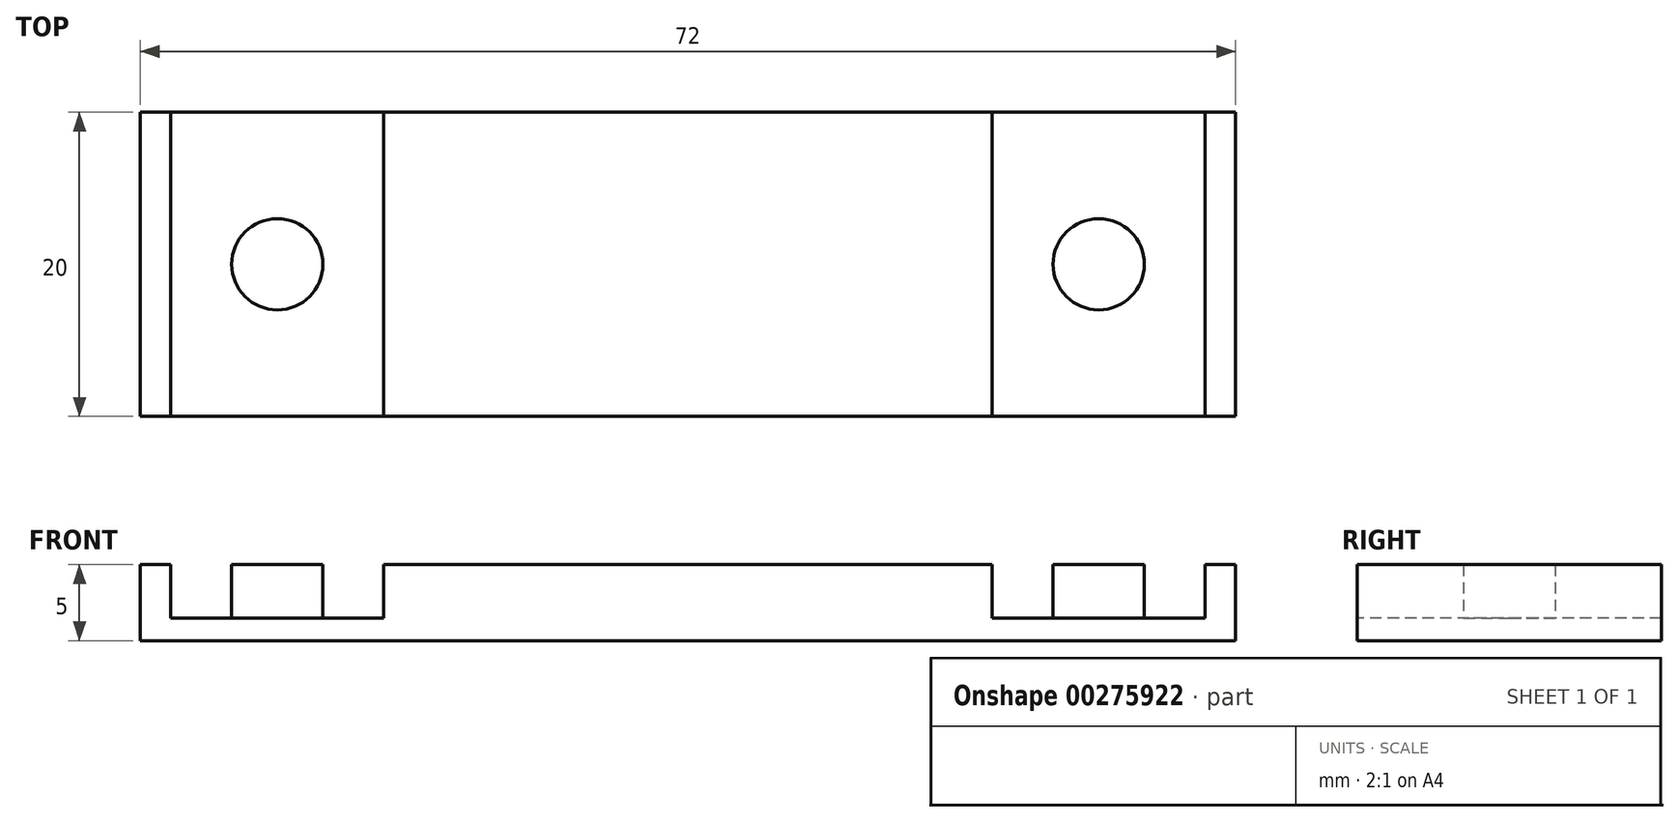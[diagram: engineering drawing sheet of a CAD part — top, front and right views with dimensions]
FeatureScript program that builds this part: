
annotation { "Feature Type Name" : "Feature", "Feature Type Description" : "" }
export const myFeature = defineFeature(function(context is Context, id is Id, definition is map)
    precondition{}
    {
        {
            var Q0;
            Q0=qCreatedBy(makeId("Top.planeOp"),FACE);
            var sketch = newSketch(context, id + "F0", { "sketchPlane" : qUnion([Q0])});
            skLineSegment(sketch, "E0.bottom", {"start": v(36, 10) * mm, "end": v(-36, 10) * mm});
            skLineSegment(sketch, "E0.top", {"start": v(36, -10) * mm, "end": v(-36, -10) * mm});
            skLineSegment(sketch, "E0.left", {"start": v(36, 10) * mm, "end": v(36, -10) * mm});
            skLineSegment(sketch, "E0.right", {"start": v(-36, 10) * mm, "end": v(-36, -10) * mm});
            skPoint(sketch, "E0.middle", {"position": v(0, 0) * mm});
            skSolve(sketch);
        }
        {
            var Q0;
            Q0=qSketchRegion(id+"F0",true);
            extrude(context, id + "F1", {"entities" : qUnion([Q0]), "depth" : 5 * mm});
        }
        {
            var Q0;
            Q0=makeQuery(id+"F1.opExtrude","CAP_FACE",FACE,{"disambiguationData":[OSD([sQuery(id+"F0.wireOp",EDGE,"E0.bottom"),sQuery(id+"F0.wireOp",EDGE,"E0.top"),sQuery(id+"F0.wireOp",EDGE,"E0.left"),sQuery(id+"F0.wireOp",EDGE,"E0.right")])],"isStart":false});
            var sketch = newSketch(context, id + "F2", { "sketchPlane" : qUnion([Q0])});
            skLineSegment(sketch, "E1.bottom", {"start": v(20, 10) * mm, "end": v(34, 10) * mm});
            skLineSegment(sketch, "E1.top", {"start": v(20, -10) * mm, "end": v(34, -10) * mm});
            skLineSegment(sketch, "E1.left", {"start": v(20, 10) * mm, "end": v(20, -10) * mm});
            skLineSegment(sketch, "E1.right", {"start": v(34, 10) * mm, "end": v(34, -10) * mm});
            skLineSegment(sketch, "E2.bottom", {"start": v(-34, 10) * mm, "end": v(-20, 10) * mm});
            skLineSegment(sketch, "E2.top", {"start": v(-34, -10) * mm, "end": v(-20, -10) * mm});
            skLineSegment(sketch, "E2.left", {"start": v(-34, 10) * mm, "end": v(-34, -10) * mm});
            skLineSegment(sketch, "E2.right", {"start": v(-20, 10) * mm, "end": v(-20, -10) * mm});
            skSolve(sketch);
        }
        {
            var Q0;
            Q0=qSketchRegion(id+"F2",true);
            extrude(context, id + "F3", {"entities" : qUnion([Q0]), "operationType" : NewBodyOperationType.REMOVE, "oppositeDirection" : true, "depth" : 3.5 * mm});
        }
        {
            var Q0;
            Q0=makeQuery(id+"F3.boolean.opBoolean","COPY",FACE,{"derivedFrom":makeQuery(id+"F3.opExtrude","CAP_FACE",FACE,{"disambiguationData":[OSD([sQuery(id+"F2.wireOp",EDGE,"E2.bottom"),sQuery(id+"F2.wireOp",EDGE,"E2.top"),sQuery(id+"F2.wireOp",EDGE,"E2.left"),sQuery(id+"F2.wireOp",EDGE,"E2.right")])],"isStart":false})});
            var sketch = newSketch(context, id + "F4", { "sketchPlane" : qUnion([Q0])});
            skLineSegment(sketch, "E3", {"start": v(-34, 10) * mm, "end": v(-20, -10) * mm, "construction": true});
            skLineSegment(sketch, "E4", {"start": v(34, -10) * mm, "end": v(20, 10) * mm, "construction": true});
            skCircle(sketch, "E5", {"center": v(-27, 0) * mm, "radius": 3 * mm});
            skPoint(sketch, "E5.perimeterSnap0", {"position": v(-27, 0) * mm});
            skCircle(sketch, "E6", {"center": v(27, 0) * mm, "radius": 3 * mm});
            skSolve(sketch);
        }
        {
            var Q0;
            Q0=qSketchRegion(id+"F4",true);
            extrude(context, id + "F5", {"entities" : qUnion([Q0]), "operationType" : NewBodyOperationType.ADD, "depth" : 3.5 * mm});
        }
    });
